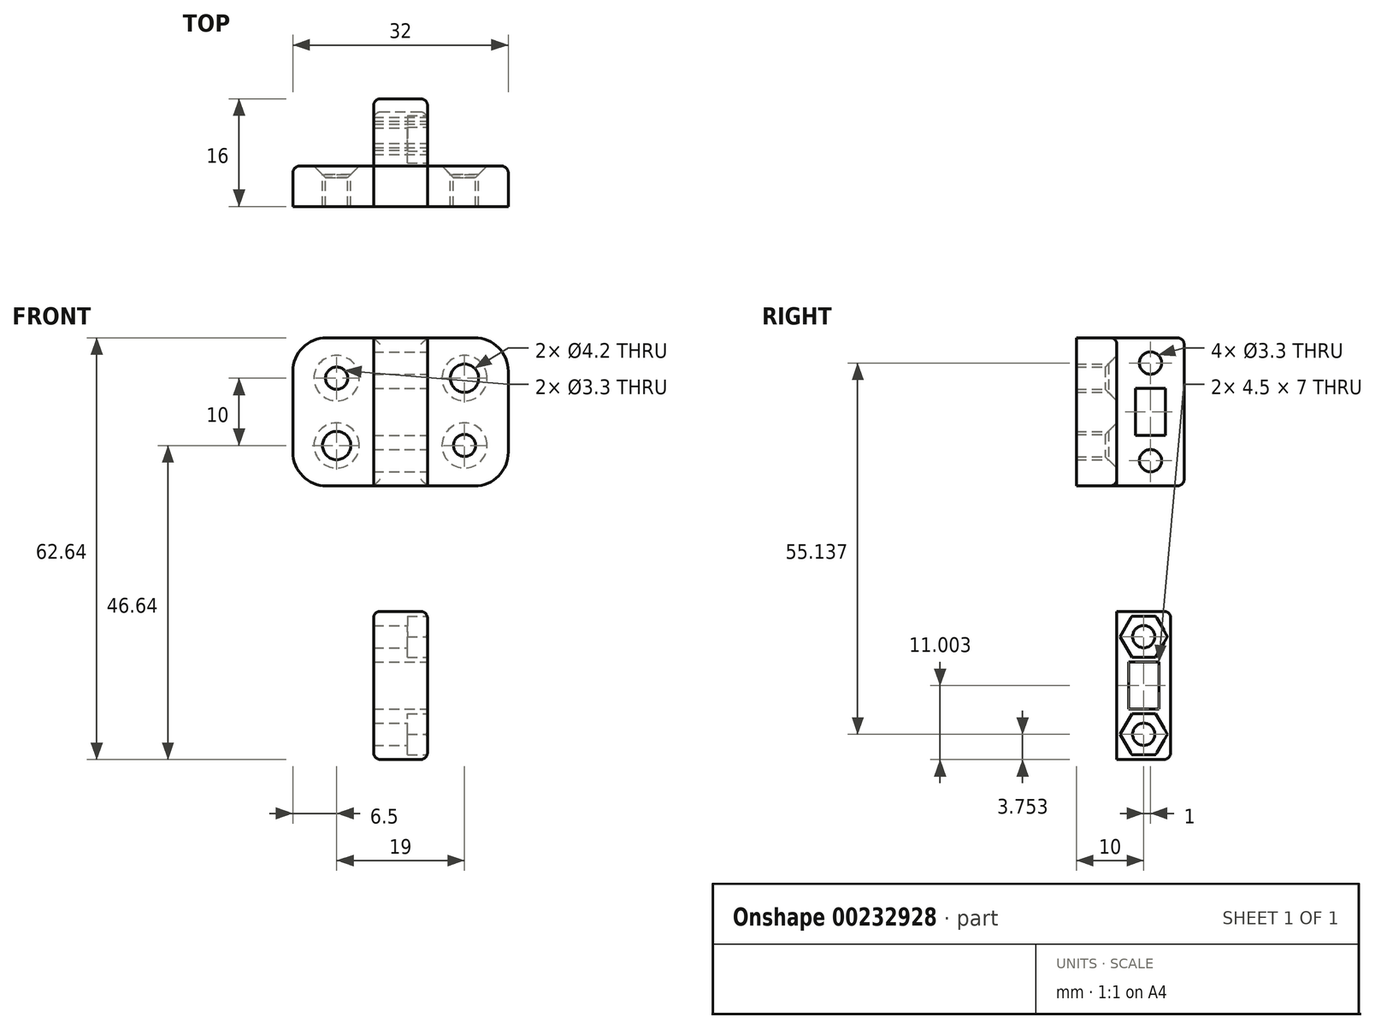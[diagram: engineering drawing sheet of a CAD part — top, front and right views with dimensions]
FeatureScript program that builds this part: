
annotation { "Feature Type Name" : "Feature", "Feature Type Description" : "" }
export const myFeature = defineFeature(function(context is Context, id is Id, definition is map)
    precondition{}
    {
        {
            var Q0;
            Q0=qCreatedBy(makeId("Front.planeOp"),FACE);
            var sketch = newSketch(context, id + "F0", { "sketchPlane" : qUnion([Q0])});
            skLineSegment(sketch, "E0.bottom", {"start": v(-16, -11) * mm, "end": v(16, -11) * mm});
            skLineSegment(sketch, "E0.top", {"start": v(-16, 11) * mm, "end": v(16, 11) * mm});
            skLineSegment(sketch, "E0.left", {"start": v(-16, -11) * mm, "end": v(-16, 11) * mm});
            skLineSegment(sketch, "E0.right", {"start": v(16, -11) * mm, "end": v(16, 11) * mm});
            skPoint(sketch, "E0.middle", {"position": v(0, 0) * mm});
            skPoint(sketch, "E1", {"position": v(-6, 11) * mm});
            skPoint(sketch, "E2", {"position": v(9.5, 0) * mm});
            skLineSegment(sketch, "E3", {"start": v(0, 0) * mm, "end": v(9.5, 0) * mm});
            skLineSegment(sketch, "E4", {"start": v(9.5, 0) * mm, "end": v(9.5, 5) * mm});
            skLineSegment(sketch, "E5", {"start": v(9.5, 0) * mm, "end": v(9.5, -5) * mm});
            skLineSegment(sketch, "E6.MirrorCS", {"start": v(-9.5, 0) * mm, "end": v(-9.5, -5) * mm});
            skLineSegment(sketch, "E7.MirrorCS", {"start": v(-9.5, 0) * mm, "end": v(-9.5, 5) * mm});
            skCircle(sketch, "E8", {"center": v(-9.5, 5) * mm, "radius": 2.1 * mm});
            skCircle(sketch, "E9.MirrorC", {"center": v(-9.5, -5) * mm, "radius": 2.1 * mm});
            skCircle(sketch, "E10.MirrorC", {"center": v(9.5, 5) * mm, "radius": 2.1 * mm});
            skCircle(sketch, "E11.MirrorC", {"center": v(9.5, -5) * mm, "radius": 2.1 * mm});
            skPoint(sketch, "E12", {"position": v(-4, 0) * mm});
            skLineSegment(sketch, "E13", {"start": v(-4, 0) * mm, "end": v(-4, 11) * mm});
            skLineSegment(sketch, "E14", {"start": v(-4, 0) * mm, "end": v(-4, -11) * mm});
            skLineSegment(sketch, "E15.MirrorCS", {"start": v(4, 0) * mm, "end": v(4, 11) * mm});
            skLineSegment(sketch, "E16.MirrorCS", {"start": v(4, 0) * mm, "end": v(4, -11) * mm});
            skSolve(sketch);
        }
        {
            var Q0;
            {var subQ0=sQuery(id+"F0.wireOp",EDGE,"E0.left");Q0=makeQuery(id+"F0.imprint","IMPRINT",FACE,{"disambiguationData":[TD([[makeQuery(id+"F0.imprint","IMPRINT",EDGE,{"derivedFrom":subQ0}),-1.0]])]});}
            var Q1;
            {var subQ0=sQuery(id+"F0.wireOp",EDGE,"E0.right");Q1=makeQuery(id+"F0.imprint","IMPRINT",FACE,{"disambiguationData":[TD([[makeQuery(id+"F0.imprint","IMPRINT",EDGE,{"derivedFrom":subQ0}),1.0]])]});}
            var Q2;
            Q2=makeQuery(id+"F0.imprint","IMPRINT",FACE,{"disambiguationData":[TD([[makeQuery(id+"F0.imprint","IMPRINT",EDGE,{"derivedFrom":sQuery(id+"F0.wireOp",EDGE,"E8")}),1.0]])]});
            var Q3;
            Q3=makeQuery(id+"F0.imprint","IMPRINT",FACE,{"disambiguationData":[TD([[makeQuery(id+"F0.imprint","IMPRINT",EDGE,{"derivedFrom":sQuery(id+"F0.wireOp",EDGE,"E10.MirrorC")}),-1.0]])]});
            var Q4;
            Q4=makeQuery(id+"F0.imprint","IMPRINT",FACE,{"disambiguationData":[TD([[makeQuery(id+"F0.imprint","IMPRINT",EDGE,{"derivedFrom":sQuery(id+"F0.wireOp",EDGE,"E11.MirrorC")}),1.0]])]});
            var Q5;
            Q5=makeQuery(id+"F0.imprint","IMPRINT",FACE,{"disambiguationData":[TD([[makeQuery(id+"F0.imprint","IMPRINT",EDGE,{"derivedFrom":sQuery(id+"F0.wireOp",EDGE,"E9.MirrorC")}),-1.0]])]});
            extrude(context, id + "F1", {"entities" : qUnion([Q0, Q1, Q2, Q3, Q4, Q5]), "depth" : 6 * mm});
        }
        {
            var Q0;
            {var subQ1=sQuery(id+"F0.wireOp",EDGE,"E13");Q0=makeQuery(id+"F0.imprint","IMPRINT",FACE,{"disambiguationData":[TD([[makeQuery(id+"F0.imprint","IMPRINT",EDGE,{"derivedFrom":subQ1}),-1.0]])]});}
            extrude(context, id + "F2", {"entities" : qUnion([Q0]), "oppositeDirection" : true, "depth" : 10 * mm});
        }
        {
            var Q0;
            {var subQ1=sQuery(id+"F0.wireOp",EDGE,"E13");Q0=makeQuery(id+"F0.imprint","IMPRINT",FACE,{"disambiguationData":[TD([[makeQuery(id+"F0.imprint","IMPRINT",EDGE,{"derivedFrom":subQ1}),-1.0]])]});}
            extrude(context, id + "F3", {"entities" : qUnion([Q0]), "depth" : 6 * mm});
        }
        {
            var Q0;
            Q0=sQuery(id+"F0.wireOp",VERTEX,"E4.end");
            var Q1;
            Q1=sQuery(id+"F0.wireOp",VERTEX,"E11.MirrorC.center");
            var Q2;
            Q2=sQuery(id+"F0.wireOp",VERTEX,"E8.center");
            var Q3;
            Q3=sQuery(id+"F0.wireOp",VERTEX,"E6.MirrorCS.end");
            var Q4;
            Q4=makeQuery(id+"F1.opExtrude","SWEPT_BODY",BODY,{"disambiguationData":[OSD([sQuery(id+"F0.wireOp",EDGE,"E0.bottom"),sQuery(id+"F0.wireOp",EDGE,"E0.top"),sQuery(id+"F0.wireOp",EDGE,"E0.right"),sQuery(id+"F0.wireOp",EDGE,"E15.MirrorCS"),sQuery(id+"F0.wireOp",EDGE,"E16.MirrorCS")])]});
            var Q5;
            Q5=makeQuery(id+"F1.opExtrude","SWEPT_BODY",BODY,{"disambiguationData":[OSD([sQuery(id+"F0.wireOp",EDGE,"E0.bottom"),sQuery(id+"F0.wireOp",EDGE,"E0.top"),sQuery(id+"F0.wireOp",EDGE,"E0.left"),sQuery(id+"F0.wireOp",EDGE,"E13"),sQuery(id+"F0.wireOp",EDGE,"E14")])]});
            hole(context, id + "F4", {"style" : HoleStyle.C_SINK, "endStyle" : HoleEndStyle.THROUGH, "oppositeDirection" : true, "standardTappedOrClearance" : lookupTablePath({ "standard" : "ISO", "fit" : "Normal", "size" : "M3", "type" : "Clearance" }), "standardBlindInLast" : lookupTablePath({ "fit" : "Standard", "standard" : "ISO", "size" : "M3", "type" : "Clearance" }), "holeDiameter" : 3.3 * mm, "cSinkDiameter" : 6.72 * mm, "cSinkAngle" : 90 * degree, "tappedDepth" : 12 * mm, "tapClearance" : 3, "locations" : qUnion([Q0, Q1, Q2, Q3]), "scope" : qUnion([Q4, Q5])});
        }
        {
            var Q0;
            Q0=makeQuery(id+"F1.opExtrude","SWEPT_EDGE",EDGE,{"disambiguationData":[OSD([sQuery(id+"F0.wireOp",EDGE,"E0.top"),sQuery(id+"F0.wireOp",EDGE,"E0.left")])]});
            var Q1;
            Q1=makeQuery(id+"F1.opExtrude","SWEPT_EDGE",EDGE,{"disambiguationData":[OSD([sQuery(id+"F0.wireOp",EDGE,"E0.bottom"),sQuery(id+"F0.wireOp",EDGE,"E0.left")])]});
            var Q2;
            Q2=makeQuery(id+"F1.opExtrude","SWEPT_EDGE",EDGE,{"disambiguationData":[OSD([sQuery(id+"F0.wireOp",EDGE,"E0.top"),sQuery(id+"F0.wireOp",EDGE,"E0.right")])]});
            var Q3;
            Q3=makeQuery(id+"F1.opExtrude","SWEPT_EDGE",EDGE,{"disambiguationData":[OSD([sQuery(id+"F0.wireOp",EDGE,"E0.bottom"),sQuery(id+"F0.wireOp",EDGE,"E0.right")])]});
            fillet(context, id + "F5", {"entities" : qUnion([Q0, Q1, Q2, Q3]), "radius" : 5 * mm, "tangentPropagation" : true, "allowEdgeOverflow" : false});
        }
        {
            var Q0;
            {var subQ0=sQuery(id+"F0.wireOp",EDGE,"E0.top");Q0=makeQuery(id+"F1.opExtrude","CAP_EDGE",EDGE,{"disambiguationData":[OSD([subQ0]),TDD([makeQuery(id+"F0.imprint","IMPRINT",EDGE,{"disambiguationData":[TD([[makeQuery(id+"F0.imprint","INTERSECT",VERTEX,{"derivedFrom":[subQ0,sQuery(id+"F0.wireOp",EDGE,"E0.left")]}),-1.0]])],"derivedFrom":subQ0})])],"isStart":true});}
            var Q1;
            {var subQ0=sQuery(id+"F0.wireOp",EDGE,"E0.right");var subQ1=sQuery(id+"F0.wireOp",EDGE,"E0.top");Q1=makeQuery(id+"F5.opFillet","BLEND_EDGE",EDGE,{"blendedFrom":[makeQuery(id+"F1.opExtrude","SWEPT_EDGE",EDGE,{"disambiguationData":[OSD([subQ1,subQ0])]}),makeQuery(id+"F1.opExtrude","CAP_FACE",FACE,{"disambiguationData":[OSD([sQuery(id+"F0.wireOp",EDGE,"E0.bottom"),subQ1,subQ0,sQuery(id+"F0.wireOp",EDGE,"E15.MirrorCS"),sQuery(id+"F0.wireOp",EDGE,"E16.MirrorCS")])],"isStart":true})],"blendedInto":[makeQuery(id+"F1.opExtrude","CAP_FACE",FACE,{"disambiguationData":[OSD([sQuery(id+"F0.wireOp",EDGE,"E0.bottom"),subQ1,subQ0,sQuery(id+"F0.wireOp",EDGE,"E15.MirrorCS"),sQuery(id+"F0.wireOp",EDGE,"E16.MirrorCS")])],"isStart":true})]});}
            fillet(context, id + "F6", {"entities" : qUnion([Q0, Q1]), "radius" : 1 * mm, "tangentPropagation" : true, "allowEdgeOverflow" : false});
        }
        {
            var Q0;
            Q0=makeQuery(id+"F2.opExtrude","SWEPT_FACE",FACE,{"disambiguationData":[OSD([sQuery(id+"F0.wireOp",EDGE,"E15.MirrorCS"),sQuery(id+"F0.wireOp",EDGE,"E16.MirrorCS")])]});
            var sketch = newSketch(context, id + "F7", { "sketchPlane" : qUnion([Q0])});
            skLineSegment(sketch, "E17", {"start": v(5, 11) * mm, "end": v(5, -11) * mm});
            skLineSegment(sketch, "E18", {"start": v(5, 0) * mm, "end": v(7.25, 0) * mm});
            skLineSegment(sketch, "E19", {"start": v(7.25, 0) * mm, "end": v(7.25, 3.5) * mm});
            skLineSegment(sketch, "E20", {"start": v(7.25, 0) * mm, "end": v(7.25, -3.5) * mm});
            skLineSegment(sketch, "E21", {"start": v(7.25, 3.5) * mm, "end": v(5, 3.5) * mm});
            skLineSegment(sketch, "E22", {"start": v(7.25, -3.5) * mm, "end": v(5, -3.5) * mm});
            skLineSegment(sketch, "E23.MirrorCS", {"start": v(2.75, 3.5) * mm, "end": v(5, 3.5) * mm});
            skLineSegment(sketch, "E24.MirrorCS", {"start": v(2.75, 0) * mm, "end": v(2.75, 3.5) * mm});
            skLineSegment(sketch, "E25.MirrorCS", {"start": v(2.75, 0) * mm, "end": v(2.75, -3.5) * mm});
            skLineSegment(sketch, "E26.MirrorCS", {"start": v(2.75, -3.5) * mm, "end": v(5, -3.5) * mm});
            skPoint(sketch, "E27", {"position": v(5, 7.25) * mm});
            skPoint(sketch, "E28", {"position": v(5, -7.25) * mm});
            skSolve(sketch);
        }
        {
            var Q0;
            {var subQ0=sQuery(id+"F7.wireOp",EDGE,"E18");Q0=makeQuery(id+"F7.imprint","IMPRINT",FACE,{"disambiguationData":[TD([[makeQuery(id+"F7.imprint","IMPRINT",EDGE,{"derivedFrom":subQ0}),1.0]])]});}
            var Q1;
            {var subQ0=sQuery(id+"F7.wireOp",EDGE,"E18");Q1=makeQuery(id+"F7.imprint","IMPRINT",FACE,{"disambiguationData":[TD([[makeQuery(id+"F7.imprint","IMPRINT",EDGE,{"derivedFrom":subQ0}),-1.0]])]});}
            var Q2;
            {var subQ0=sQuery(id+"F7.wireOp",EDGE,"E23.MirrorCS");Q2=makeQuery(id+"F7.imprint","IMPRINT",FACE,{"disambiguationData":[TD([[makeQuery(id+"F7.imprint","IMPRINT",EDGE,{"derivedFrom":subQ0}),-1.0]])]});}
            extrude(context, id + "F8", {"entities" : qUnion([Q0, Q1, Q2]), "operationType" : NewBodyOperationType.REMOVE, "oppositeDirection" : true, "depth" : 25 * mm});
        }
        {
            var Q0;
            Q0=sQuery(id+"F7.wireOp",VERTEX,"E27");
            var Q1;
            Q1=sQuery(id+"F7.wireOp",VERTEX,"E28");
            var Q2;
            Q2=makeQuery(id+"F2.opExtrude","SWEPT_BODY",BODY,{"disambiguationData":[OSD([sQuery(id+"F0.wireOp",EDGE,"E0.bottom"),sQuery(id+"F0.wireOp",EDGE,"E0.top"),sQuery(id+"F0.wireOp",EDGE,"E13"),sQuery(id+"F0.wireOp",EDGE,"E14"),sQuery(id+"F0.wireOp",EDGE,"E15.MirrorCS"),sQuery(id+"F0.wireOp",EDGE,"E16.MirrorCS")])]});
            hole(context, id + "F9", {"style" : HoleStyle.SIMPLE, "endStyle" : HoleEndStyle.THROUGH, "standardTappedOrClearance" : lookupTablePath({ "standard" : "ISO", "fit" : "Normal", "size" : "M3", "type" : "Clearance" }), "standardBlindInLast" : lookupTablePath({ "fit" : "Standard", "standard" : "ISO", "size" : "M3", "type" : "Clearance" }), "holeDiameter" : 3.3 * mm, "tappedDepth" : 12 * mm, "tapClearance" : 3, "locations" : qUnion([Q0, Q1]), "scope" : qUnion([Q2])});
        }
        {
            var Q0;
            Q0=makeQuery(id+"F2.opExtrude","CAP_EDGE",EDGE,{"disambiguationData":[OSD([sQuery(id+"F0.wireOp",EDGE,"E15.MirrorCS"),sQuery(id+"F0.wireOp",EDGE,"E16.MirrorCS")])],"isStart":false});
            var Q1;
            Q1=makeQuery(id+"F2.opExtrude","CAP_EDGE",EDGE,{"disambiguationData":[OSD([sQuery(id+"F0.wireOp",EDGE,"E0.top")])],"isStart":false});
            var Q2;
            Q2=makeQuery(id+"F2.opExtrude","CAP_EDGE",EDGE,{"disambiguationData":[OSD([sQuery(id+"F0.wireOp",EDGE,"E13"),sQuery(id+"F0.wireOp",EDGE,"E14")])],"isStart":false});
            var Q3;
            Q3=makeQuery(id+"F2.opExtrude","CAP_EDGE",EDGE,{"disambiguationData":[OSD([sQuery(id+"F0.wireOp",EDGE,"E0.bottom")])],"isStart":false});
            fillet(context, id + "F10", {"entities" : qUnion([Q0, Q1, Q2, Q3]), "radius" : 1 * mm, "tangentPropagation" : true, "allowEdgeOverflow" : false});
        }
        {
            var Q0;
            Q0=qCreatedBy(makeId("Front.planeOp"),FACE);
            var sketch = newSketch(context, id + "F11", { "sketchPlane" : qUnion([Q0])});
            skLineSegment(sketch, "E29.bottom", {"start": v(4, -29.64) * mm, "end": v(-4, -29.64) * mm});
            skLineSegment(sketch, "E29.top", {"start": v(4, -51.64) * mm, "end": v(-4, -51.64) * mm});
            skLineSegment(sketch, "E29.left", {"start": v(4, -29.64) * mm, "end": v(4, -51.64) * mm});
            skLineSegment(sketch, "E29.right", {"start": v(-4, -29.64) * mm, "end": v(-4, -51.64) * mm});
            skPoint(sketch, "E29.middle", {"position": v(0, -40.64) * mm});
            skSolve(sketch);
        }
        {
            var Q0;
            Q0 = qSketchRegion(id + "F11", true);
            extrude(context, id + "F12", {"entities" : qUnion([Q0]), "oppositeDirection" : true, "depth" : 8 * mm});
        }
        {
            var Q0;
            Q0=makeQuery(id+"F12.opExtrude","SWEPT_FACE",FACE,{"disambiguationData":[OSD([sQuery(id+"F11.wireOp",EDGE,"E29.left")])]});
            var sketch = newSketch(context, id + "F13", { "sketchPlane" : qUnion([Q0])});
            skLineSegment(sketch, "E30", {"start": v(4, -29.64) * mm, "end": v(4, -51.64) * mm});
            skLineSegment(sketch, "E31", {"start": v(4, -40.64) * mm, "end": v(6.25, -40.64) * mm});
            skLineSegment(sketch, "E32", {"start": v(6.25, -40.64) * mm, "end": v(6.25, -37.14) * mm});
            skLineSegment(sketch, "E33", {"start": v(6.25, -40.64) * mm, "end": v(6.25, -44.14) * mm});
            skLineSegment(sketch, "E34", {"start": v(6.25, -37.14) * mm, "end": v(4, -37.14) * mm});
            skLineSegment(sketch, "E35", {"start": v(6.25, -44.14) * mm, "end": v(4, -44.14) * mm});
            skLineSegment(sketch, "E36.MirrorCS", {"start": v(1.75, -37.14) * mm, "end": v(4, -37.14) * mm});
            skLineSegment(sketch, "E37.MirrorCS", {"start": v(1.75, -40.64) * mm, "end": v(1.75, -37.14) * mm});
            skLineSegment(sketch, "E38.MirrorCS", {"start": v(1.75, -40.64) * mm, "end": v(1.75, -44.14) * mm});
            skLineSegment(sketch, "E39.MirrorCS", {"start": v(1.75, -44.14) * mm, "end": v(4, -44.14) * mm});
            skPoint(sketch, "E40", {"position": v(4, -33.39) * mm});
            skPoint(sketch, "E41", {"position": v(4, -47.89) * mm});
            skCircle(sketch, "E42.cCircle", {"center": v(4, -33.39) * mm, "radius": 3.05 * mm, "construction": true});
            skLineSegment(sketch, "E42.0", {"start": v(2.24, -30.34) * mm, "end": v(5.76, -30.34) * mm});
            skLineSegment(sketch, "E42.1", {"start": v(5.76, -30.34) * mm, "end": v(7.52, -33.39) * mm});
            skLineSegment(sketch, "E42.2", {"start": v(7.52, -33.39) * mm, "end": v(5.76, -36.44) * mm});
            skLineSegment(sketch, "E42.3", {"start": v(5.76, -36.44) * mm, "end": v(2.24, -36.44) * mm});
            skLineSegment(sketch, "E42.4", {"start": v(2.24, -36.44) * mm, "end": v(0.48, -33.39) * mm});
            skLineSegment(sketch, "E42.5", {"start": v(0.48, -33.39) * mm, "end": v(2.24, -30.34) * mm});
            skPoint(sketch, "E42.0.midPoint", {"position": v(4, -30.34) * mm});
            skCircle(sketch, "E43.cCircle", {"center": v(4, -47.89) * mm, "radius": 3.05 * mm, "construction": true});
            skLineSegment(sketch, "E43.0", {"start": v(5.76, -50.94) * mm, "end": v(2.24, -50.94) * mm});
            skLineSegment(sketch, "E43.1", {"start": v(2.24, -50.94) * mm, "end": v(0.48, -47.89) * mm});
            skLineSegment(sketch, "E43.2", {"start": v(0.48, -47.89) * mm, "end": v(2.24, -44.84) * mm});
            skLineSegment(sketch, "E43.3", {"start": v(2.24, -44.84) * mm, "end": v(5.76, -44.84) * mm});
            skLineSegment(sketch, "E43.4", {"start": v(5.76, -44.84) * mm, "end": v(7.52, -47.89) * mm});
            skLineSegment(sketch, "E43.5", {"start": v(7.52, -47.89) * mm, "end": v(5.76, -50.94) * mm});
            skPoint(sketch, "E43.0.midPoint", {"position": v(4, -50.94) * mm});
            skSolve(sketch);
        }
        {
            var Q0;
            Q0=sQuery(id+"F13.wireOp",VERTEX,"E40");
            var Q1;
            Q1=sQuery(id+"F13.wireOp",VERTEX,"E41");
            var Q2;
            Q2=makeQuery(id+"F12.opExtrude","SWEPT_BODY",BODY,{"disambiguationData":[OSD([sQuery(id+"F11.wireOp",EDGE,"E29.bottom"),sQuery(id+"F11.wireOp",EDGE,"E29.top"),sQuery(id+"F11.wireOp",EDGE,"E29.left"),sQuery(id+"F11.wireOp",EDGE,"E29.right")])]});
            hole(context, id + "F14", {"style" : HoleStyle.SIMPLE, "endStyle" : HoleEndStyle.THROUGH, "standardTappedOrClearance" : lookupTablePath({ "standard" : "ISO", "fit" : "Normal", "size" : "M3", "type" : "Clearance" }), "standardBlindInLast" : lookupTablePath({ "fit" : "Standard", "standard" : "ISO", "size" : "M3", "type" : "Clearance" }), "holeDiameter" : 3.3 * mm, "tappedDepth" : 12 * mm, "tapClearance" : 3, "locations" : qUnion([Q0, Q1]), "scope" : qUnion([Q2])});
        }
        {
            var Q0;
            {var subQ0=sQuery(id+"F13.wireOp",EDGE,"E36.MirrorCS");Q0=makeQuery(id+"F13.imprint","IMPRINT",FACE,{"disambiguationData":[TD([[makeQuery(id+"F13.imprint","IMPRINT",EDGE,{"derivedFrom":subQ0}),-1.0]])]});}
            var Q1;
            {var subQ0=sQuery(id+"F13.wireOp",EDGE,"E31");Q1=makeQuery(id+"F13.imprint","IMPRINT",FACE,{"disambiguationData":[TD([[makeQuery(id+"F13.imprint","IMPRINT",EDGE,{"derivedFrom":subQ0}),-1.0]])]});}
            var Q2;
            {var subQ0=sQuery(id+"F13.wireOp",EDGE,"E31");Q2=makeQuery(id+"F13.imprint","IMPRINT",FACE,{"disambiguationData":[TD([[makeQuery(id+"F13.imprint","IMPRINT",EDGE,{"derivedFrom":subQ0}),1.0]])]});}
            extrude(context, id + "F15", {"entities" : qUnion([Q0, Q1, Q2]), "operationType" : NewBodyOperationType.REMOVE, "oppositeDirection" : true, "depth" : 25 * mm});
        }
        {
            var Q0;
            Q0=makeQuery(id+"F12.opExtrude","SWEPT_EDGE",EDGE,{"disambiguationData":[OSD([sQuery(id+"F11.wireOp",EDGE,"E29.bottom"),sQuery(id+"F11.wireOp",EDGE,"E29.left")])]});
            var Q1;
            Q1=makeQuery(id+"F12.opExtrude","SWEPT_EDGE",EDGE,{"disambiguationData":[OSD([sQuery(id+"F11.wireOp",EDGE,"E29.bottom"),sQuery(id+"F11.wireOp",EDGE,"E29.right")])]});
            var Q2;
            Q2=makeQuery(id+"F12.opExtrude","SWEPT_EDGE",EDGE,{"disambiguationData":[OSD([sQuery(id+"F11.wireOp",EDGE,"E29.top"),sQuery(id+"F11.wireOp",EDGE,"E29.left")])]});
            var Q3;
            Q3=makeQuery(id+"F12.opExtrude","CAP_EDGE",EDGE,{"disambiguationData":[OSD([sQuery(id+"F11.wireOp",EDGE,"E29.top")])],"isStart":false});
            var Q4;
            Q4=makeQuery(id+"F12.opExtrude","CAP_EDGE",EDGE,{"disambiguationData":[OSD([sQuery(id+"F11.wireOp",EDGE,"E29.left")])],"isStart":false});
            var Q5;
            Q5=makeQuery(id+"F12.opExtrude","CAP_EDGE",EDGE,{"disambiguationData":[OSD([sQuery(id+"F11.wireOp",EDGE,"E29.bottom")])],"isStart":false});
            var Q6;
            Q6=makeQuery(id+"F12.opExtrude","CAP_EDGE",EDGE,{"disambiguationData":[OSD([sQuery(id+"F11.wireOp",EDGE,"E29.right")])],"isStart":false});
            var Q7;
            Q7=makeQuery(id+"F12.opExtrude","SWEPT_EDGE",EDGE,{"disambiguationData":[OSD([sQuery(id+"F11.wireOp",EDGE,"E29.top"),sQuery(id+"F11.wireOp",EDGE,"E29.right")])]});
            fillet(context, id + "F16", {"entities" : qUnion([Q0, Q1, Q2, Q3, Q4, Q5, Q6, Q7]), "radius" : 1 * mm, "tangentPropagation" : true, "allowEdgeOverflow" : false});
        }
        {
            var Q0;
            {var subQ1=sQuery(id+"F13.wireOp",EDGE,"E42.1");Q0=makeQuery(id+"F13.imprint","IMPRINT",FACE,{"disambiguationData":[TD([[makeQuery(id+"F13.imprint","IMPRINT",EDGE,{"derivedFrom":subQ1}),-1.0]])]});}
            var Q1;
            {var subQ0=sQuery(id+"F13.wireOp",EDGE,"E42.4");Q1=makeQuery(id+"F13.imprint","IMPRINT",FACE,{"disambiguationData":[TD([[makeQuery(id+"F13.imprint","IMPRINT",EDGE,{"derivedFrom":subQ0}),-1.0]])]});}
            var Q2;
            {var subQ0=sQuery(id+"F13.wireOp",EDGE,"E43.4");Q2=makeQuery(id+"F13.imprint","IMPRINT",FACE,{"disambiguationData":[TD([[makeQuery(id+"F13.imprint","IMPRINT",EDGE,{"derivedFrom":subQ0}),-1.0]])]});}
            var Q3;
            {var subQ6=sQuery(id+"F13.wireOp",EDGE,"E43.1");Q3=makeQuery(id+"F13.imprint","IMPRINT",FACE,{"disambiguationData":[TD([[makeQuery(id+"F13.imprint","IMPRINT",EDGE,{"derivedFrom":subQ6}),-1.0]])]});}
            extrude(context, id + "F17", {"entities" : qUnion([Q0, Q1, Q2, Q3]), "operationType" : NewBodyOperationType.REMOVE, "oppositeDirection" : true, "depth" : 3 * mm});
        }
    });
